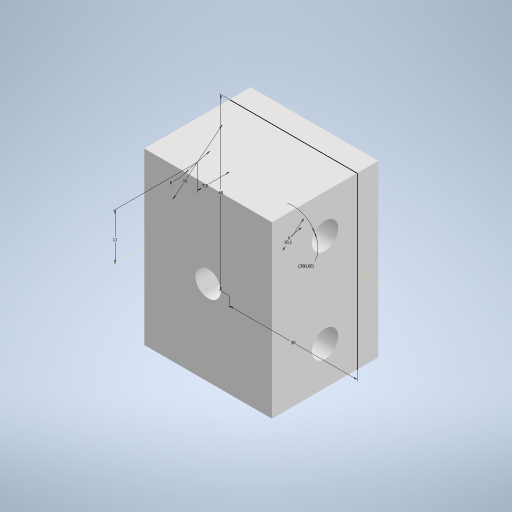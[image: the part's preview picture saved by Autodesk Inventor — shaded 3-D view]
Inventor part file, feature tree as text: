
AUTODESK INVENTOR PART (.ipt)
format: ipt  version: 2024.2 (Build 282272000, 272)  size: 266,752 bytes
history: native  units: mm
features: extrude x3, sketch x2, other x1, fillet x1, hole x1
ambient origin geometry x8: Origin, YZ Plane, XZ Plane, XY Plane, X Axis, Y Axis, Z Axis, Center Point
bodies: Body1 (feature_tree)
feature tree (8):
  other  "Bryła1"
  sketch  "Szkic1"
  extrude  "Wyciągnięcie proste1"  Depth=6.0mm
  extrude  "Wyciągnięcie proste2"  Depth=10.1mm
  fillet  "Zaokrąglenie1"  Radius=30.0mm
  sketch  "Szkic2"
  extrude  "Wyciągnięcie proste3"  Depth=40.0mm
  hole  "Otwór1"  [1 undecoded]
note: 1 required parameter value undecoded (feature->parameter linkage not recoverable at this tier; creation-order binding heuristic only, values carry confidence <= 0.55)
